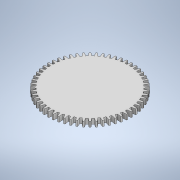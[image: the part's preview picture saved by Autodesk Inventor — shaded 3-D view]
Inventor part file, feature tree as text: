
AUTODESK INVENTOR PART (.ipt)
format: ipt  version: 2020 (Build 240168000, 168)  size: 380,928 bytes
history: native  units: in
note: dims shown in document units (in); Inventor stores cm internally (conversion verified against a paired STEP export)
features: extrude x1, sketch x1
ambient origin geometry x8: Origin, YZ Plane, XZ Plane, XY Plane, X Axis, Y Axis, Z Axis, Center Point
bodies: Body1 (feature_tree)
feature tree (2):
  extrude  "Extrusion2"  Depth=0.1575in
  sketch  "Sketch1"  dims[d0=2.5984in d4=2.3622in d9=22.0472in d11=360.0deg d13=0.1575in d14=0.0in]
